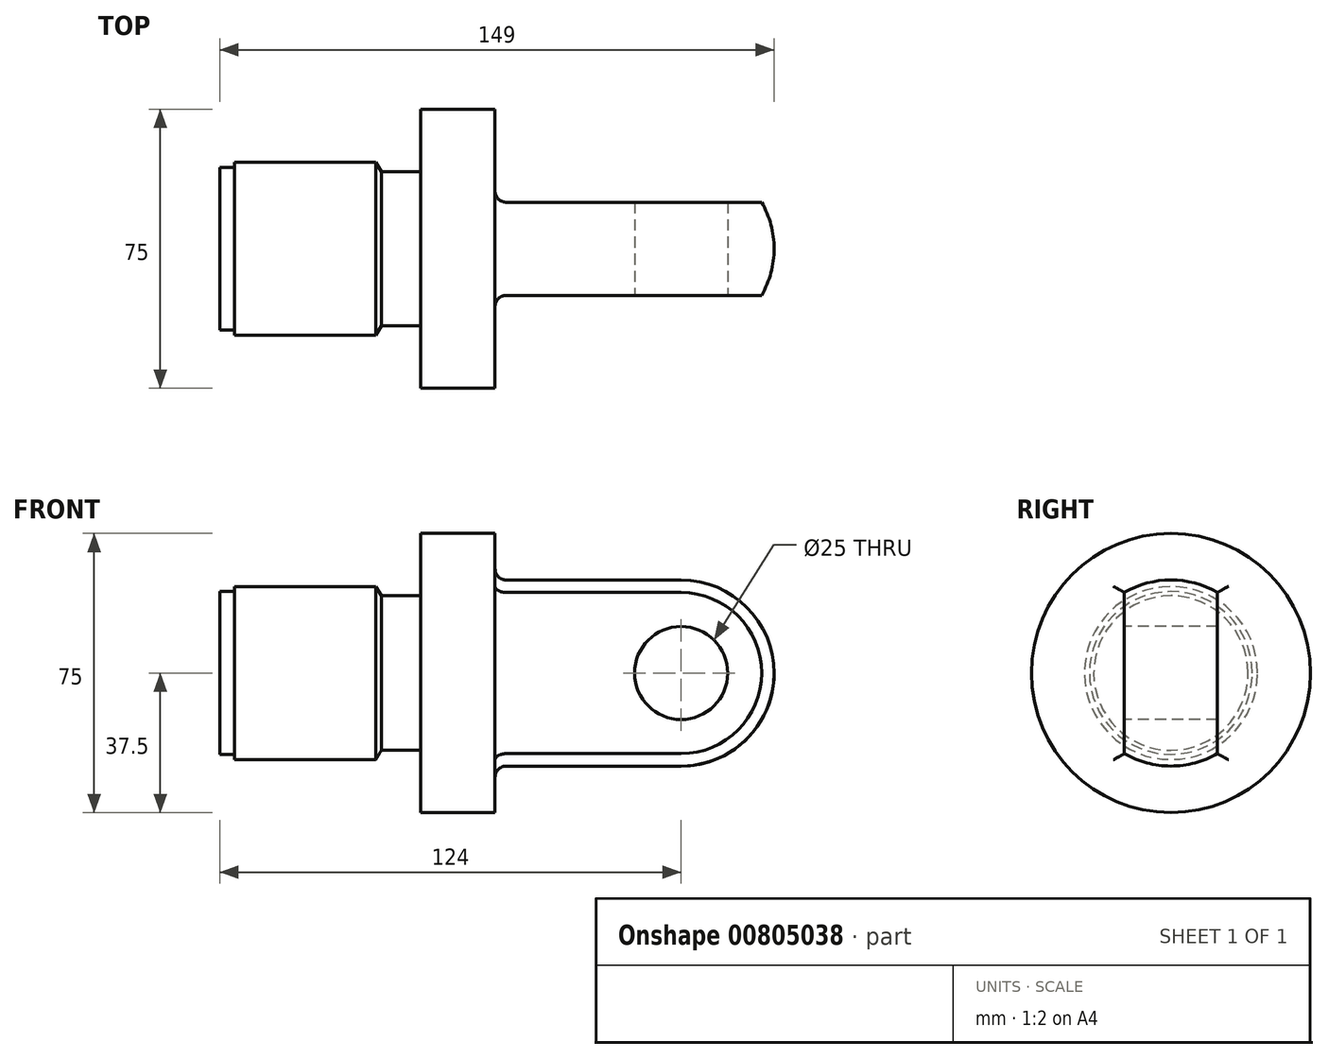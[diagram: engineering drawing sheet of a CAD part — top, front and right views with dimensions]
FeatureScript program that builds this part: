
annotation { "Feature Type Name" : "Feature", "Feature Type Description" : "" }
export const myFeature = defineFeature(function(context is Context, id is Id, definition is map)
    precondition{}
    {
        {
            assignVariable(context, id + "F0", {"name" : "luglenghth", "anyValue" : 75});
        }
        {
            var Q0;
            Q0=qCreatedBy(makeId("Front.planeOp"),FACE);
            var sketch = newSketch(context, id + "F1", { "sketchPlane" : qUnion([Q0])});
            skLineSegment(sketch, "E0", {"start": v(0, 0) * mm, "end": v(0, 23.25) * mm});
            skLineSegment(sketch, "E1", {"start": v(0, 23.25) * mm, "end": v(38, 23.25) * mm});
            skLineSegment(sketch, "E2", {"start": v(38, 23.25) * mm, "end": v(38, 20.75) * mm});
            skLineSegment(sketch, "E3", {"start": v(38, 20.75) * mm, "end": v(50, 20.75) * mm});
            skLineSegment(sketch, "E4", {"start": v(50, 20.75) * mm, "end": v(50, 37.5) * mm});
            skLineSegment(sketch, "E5", {"start": v(50, 37.5) * mm, "end": v(70, 37.5) * mm});
            skLineSegment(sketch, "E6", {"start": v(70, 37.5) * mm, "end": v(70, 25) * mm});
            skLineSegment(sketch, "E7", {"start": v(70, 25) * mm, "end": v(120, 25) * mm});
            skLineSegment(sketch, "E8", {"start": v(145, 0) * mm, "end": v(145, 0) * mm});
            skLineSegment(sketch, "E9", {"start": v(145, 0) * mm, "end": v(0, 0) * mm});
            skLineSegment(sketch, "E10", {"start": v(38, 23.25) * mm, "end": v(39.44, 20.75) * mm});
            skLineSegment(sketch, "E11", {"start": v(0, 21.87) * mm, "end": v(-4, 21.87) * mm});
            skLineSegment(sketch, "E12", {"start": v(-4, 21.87) * mm, "end": v(-4, 0) * mm});
            skLineSegment(sketch, "E13", {"start": v(-4, 0) * mm, "end": v(0, 0) * mm});
            skPoint(sketch, "E14.visualSharp", {"position": v(145, 25) * mm});
            skArc(sketch, "E14.filletArc", {"start": v(145, 0) * mm, "mid": v(137.68, 17.68) * mm, "end": v(120, 25) * mm});
            skSolve(sketch);
        }
        {
            var Q0;
            Q0=makeQuery(id+"F1.imprint","IMPRINT",FACE,{"disambiguationData":[TD([[makeQuery(id+"F1.imprint","IMPRINT",EDGE,{"derivedFrom":sQuery(id+"F1.wireOp",EDGE,"E0")}),-1.0]])]});
            var Q1;
            {var subQ3=sQuery(id+"F1.wireOp",EDGE,"oPnuAlFy-IrYi-2yoG-jHFL-xciEVcSRY0PP");Q1=makeQuery(id+"F1.imprint","IMPRINT",FACE,{"disambiguationData":[TD([[makeQuery(id+"F1.imprint","IMPRINT",EDGE,{"derivedFrom":subQ3}),1.0]])]});}
            var Q2;
            {var subQ0=sQuery(id+"F1.wireOp",EDGE,"E2");Q2=makeQuery(id+"F1.imprint","IMPRINT",FACE,{"disambiguationData":[TD([[makeQuery(id+"F1.imprint","IMPRINT",EDGE,{"derivedFrom":subQ0}),1.0]])]});}
            var Q3;
            {var subQ3=sQuery(id+"F1.wireOp",EDGE,"csDcFAml-2kwJ-iulf-wmFu-xSCYByRtuIZr");Q3=makeQuery(id+"F1.imprint","IMPRINT",FACE,{"disambiguationData":[TD([[makeQuery(id+"F1.imprint","IMPRINT",EDGE,{"derivedFrom":subQ3}),1.0]])]});}
            var Q4;
            {var subQ2=sQuery(id+"F1.wireOp",EDGE,"E11");Q4=makeQuery(id+"F1.imprint","IMPRINT",FACE,{"disambiguationData":[TD([[makeQuery(id+"F1.imprint","IMPRINT",EDGE,{"derivedFrom":subQ2}),1.0]])]});}
            var Q5;
            Q5=sQuery(id+"F1.wireOp",EDGE,"E9");
            revolve(context, id + "F2", {"surfaceOperationType" : NewSurfaceOperationType.NEW, "entities" : qUnion([Q0, Q1, Q2, Q3, Q4]), "axis" : qUnion([Q5]), "revolveType" : RevolveType.FULL});
        }
        {
            var Q0;
            Q0=makeQuery(id+"F2.opRevolve","SWEPT_FACE",FACE,{"disambiguationData":[OSD([sQuery(id+"F1.wireOp",EDGE,"E6")])]});
            var sketch = newSketch(context, id + "F3", { "sketchPlane" : qUnion([Q0])});
            skLineSegment(sketch, "E15.bottom", {"start": v(-12.5, 21.65) * mm, "end": v(-37.5, 21.65) * mm});
            skLineSegment(sketch, "E15.top", {"start": v(-12.5, -21.65) * mm, "end": v(-37.5, -21.65) * mm});
            skLineSegment(sketch, "E15.left", {"start": v(-12.5, 21.65) * mm, "end": v(-12.5, -21.65) * mm});
            skLineSegment(sketch, "E15.right", {"start": v(-37.5, 21.65) * mm, "end": v(-37.5, -21.65) * mm});
            skLineSegment(sketch, "E16.bottom", {"start": v(12.5, 21.65) * mm, "end": v(37.5, 21.65) * mm});
            skLineSegment(sketch, "E16.top", {"start": v(12.5, -21.65) * mm, "end": v(37.5, -21.65) * mm});
            skLineSegment(sketch, "E16.left", {"start": v(12.5, 21.65) * mm, "end": v(12.5, -21.65) * mm});
            skLineSegment(sketch, "E16.right", {"start": v(37.5, 21.65) * mm, "end": v(37.5, -21.65) * mm});
            skSolve(sketch);
        }
        {
            var Q0;
            Q0=qSketchRegion(id+"F3",true);
            var Q1;
            Q1=makeQuery(id+"F2.opRevolve","SWEPT_FACE",FACE,{"disambiguationData":[OSD([sQuery(id+"F1.wireOp",EDGE,"E8")])]});
            extrude(context, id + "F4", {"entities" : qUnion([Q0]), "operationType" : NewBodyOperationType.REMOVE, "depth" : (getVariable(context, 'luglenghth')) * mm, "endBoundEntityFace" : qUnion([Q1]), "offsetDistance" : 25 * mm});
        }
        {
            var Q0;
            Q0=makeQuery(id+"F4.boolean.opBoolean","COPY",FACE,{"derivedFrom":makeQuery(id+"F4.opExtrude","SWEPT_FACE",FACE,{"disambiguationData":[OSD([sQuery(id+"F3.wireOp",EDGE,"E15.left")])]})});
            var sketch = newSketch(context, id + "F5", { "sketchPlane" : qUnion([Q0])});
            skCircle(sketch, "E17", {"center": v(120, 0) * mm, "radius": 12.5 * mm});
            skSolve(sketch);
        }
        {
            var Q0;
            Q0=qSketchRegion(id+"F5",true);
            var Q1;
            Q1=makeQuery(id+"F4.boolean.opBoolean","COPY",FACE,{"derivedFrom":makeQuery(id+"F4.opExtrude","SWEPT_FACE",FACE,{"disambiguationData":[OSD([sQuery(id+"F3.wireOp",EDGE,"E16.left")])]})});
            extrude(context, id + "F6", {"entities" : qUnion([Q0]), "operationType" : NewBodyOperationType.REMOVE, "endBound" : BoundingType.UP_TO_SURFACE, "oppositeDirection" : true, "depth" : 25 * mm, "endBoundEntityFace" : qUnion([Q1]), "offsetDistance" : 25 * mm});
        }
        {
            var Q0;
            Q0=makeQuery(id+"F4.boolean.opBoolean","COPY",EDGE,{"derivedFrom":makeQuery(id+"F4.opExtrude","CAP_EDGE",EDGE,{"disambiguationData":[OSD([sQuery(id+"F3.wireOp",EDGE,"E15.left")])],"isStart":true})});
            var Q1;
            Q1=makeQuery(id+"F4.boolean.opBoolean","COPY",EDGE,{"derivedFrom":makeQuery(id+"F4.opExtrude","CAP_EDGE",EDGE,{"disambiguationData":[OSD([sQuery(id+"F3.wireOp",EDGE,"E16.left")])],"isStart":true})});
            var Q2;
            Q2=makeQuery(id+"F4.boolean.opBoolean","SPLIT",EDGE,{"disambiguationData":[OD(0.0)],"derivedFrom":makeQuery(id+"F2.opRevolve","SWEPT_EDGE",EDGE,{"disambiguationData":[OSD([sQuery(id+"F1.wireOp",EDGE,"E6"),sQuery(id+"F1.wireOp",EDGE,"E7")])]})});
            var Q3;
            Q3=makeQuery(id+"F4.boolean.opBoolean","SPLIT",EDGE,{"disambiguationData":[OD(1.0)],"derivedFrom":makeQuery(id+"F2.opRevolve","SWEPT_EDGE",EDGE,{"disambiguationData":[OSD([sQuery(id+"F1.wireOp",EDGE,"E6"),sQuery(id+"F1.wireOp",EDGE,"E7")])]})});
            fillet(context, id + "F7", {"entities" : qUnion([Q0, Q1, Q2, Q3]), "radius" : 3 * mm, "tangentPropagation" : true, "allowEdgeOverflow" : false});
        }
    });
